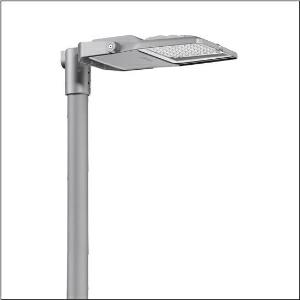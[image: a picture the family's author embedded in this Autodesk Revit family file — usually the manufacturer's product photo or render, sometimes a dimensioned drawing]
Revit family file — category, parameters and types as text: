
# Revit family: floodlight_fl_21_iq_mini___pl43_5xa7772c2a3a_c494
name_source: partatom
category: Lighting Fixtures
units: mm (PartAtom-declared; Revit-internal decimal feet)

## family parameters
Cut with Voids When Loaded = No
Host = Face
Light Source = No
Part Type = Normal
Room Calculation Point = No
Round Connector Dimension = Use Diameter
Shared = No

## types (1)
- --- (1 x LED, 12520 lm, 87.2 W, 3000K)
    Apparent Load = 87 VA
    CIE Flux Codes = 27 78 99 100 100
    Color Rendering = 70
    Color Temperature = 3000K
    Default Elevation = 1800 mm
    Description = Floodlight FL 21 iQ mini, floodlight, primary light control with lens, of PMMA, primary optical cover: protective disc, of toughened safety glass, transparent, light distribution: PL43, light emission: direct distribution, installation type: surface-mounted, LED, High Power LED, rated luminous flux: 12.520lm, luminous efficacy: 144lm/W, light colour: 730, colour temperature: 3000K, control: Auto-Match, Temp-Guard, Night-Set, Smart-Wire, Desk-Remote (wireless, voltage-free reading and setting of iQ features in the workshop via application-optimized NFC function/RFID function), optimised constant luminous flux control (CLO 2.0), Light-Fading, Lumen-Switch, with terminal, 6-pole, mains connection: 220..240V, AC, 50/60Hz, start of lifetime: 87W, end of service life: 92W, reduction: 40W, luminaire housing, of diecast aluminium, powder-coated, Siteco® metallic grey (DB 702S), corrosivity category C5 mid according to DIN EN ISO 12944, sealing non-destructively replaceable, please order mast flange separately, mast bracket, of steel, galvanised, powder-coated, protection rating (complete): IP66, insulation class (complete): insulation class II (safety insulation), certification: CE, ENEC, VDE, protection symbol: D, impact resistance: IK08, permissible operating ambient temperature: -40..+40°C, permissible operating ambient temperature for outdoor applications: -40..+50°C, standard: DIN EN 12944, LABS conformity tested according to VDMA 24364:2018-05, packaging unit: 1 piece

Light Distribution: PL43
    Height = 70 mm
    Lamp = 1 x LED
    Lamp Light Flux = 12520 lm
    Lamp Power = 87.2 W
    Lamp count = 1
    Length = 485 mm
    Luminous efficacy = 144 lm/W
    Manufacturer = Siteco
    ModVariant = No
    Model = 5XA7772C2A3A
    Number of Poles = 1
    OnlyDefault = Yes
    Power Factor = 1
    Product Name = Floodlight FL 21 iQ mini | PL43
    Product group = floodlight | pylon annexe
    ProductGroupID = 6200
    Protection Class = Protection class II
    Protection Degree = IP 66
    RLX_Detail_Level = 1
    RLX_Emergency_Light_Flux = 0 lm
    RLX_Emergency_Type = 0
    RLX_Emergency_Type_DB = No
    RlxData = <blob elided: 101161 chars, md5=ba0d7f5b>
    Socket = socket
    Standby Power = 0 W
    System Light Flux = 12520 lm
    System Power = 87 W
    Type Comments = factory setting: luminous flux: 100 % | dim-lin: 254 | 456 mA
    Type Image = l_1007125.jpg
    URL = http://relux.com
    VarID = @adj_112457
    Voltage = 0 V
    Weight = 0.00 kg
    Width = 337 mm

## geometry (parser evidence)
native form markers: Blend x4, Sweep x13
no freeform markers — native parametric forms only
